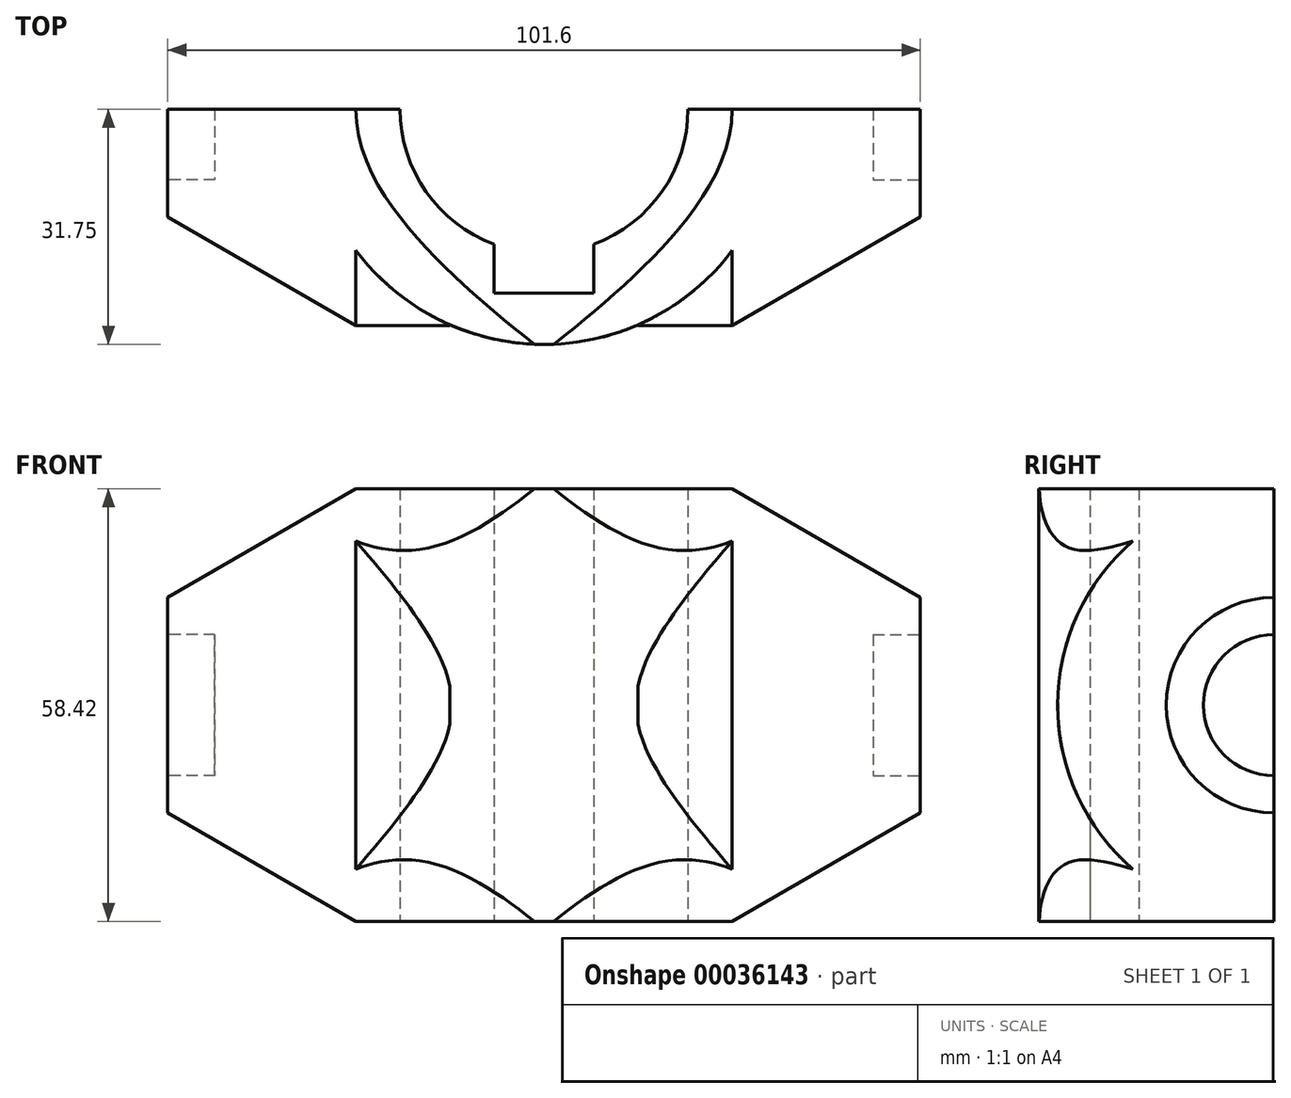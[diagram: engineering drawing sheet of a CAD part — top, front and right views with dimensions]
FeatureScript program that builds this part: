
annotation { "Feature Type Name" : "Feature", "Feature Type Description" : "" }
export const myFeature = defineFeature(function(context is Context, id is Id, definition is map)
    precondition{}
    {
        {
            var Q0;
            Q0=qCreatedBy(makeId("Top.planeOp"),FACE);
            var sketch = newSketch(context, id + "F0", { "sketchPlane" : qUnion([Q0])});
            skPoint(sketch, "E0.rect.middle", {"position": v(0, 0) * mm});
            skArc(sketch, "E1", {"start": v(-31.75, 0) * mm, "mid": v(0, -31.75) * mm, "end": v(31.75, 0) * mm});
            skLineSegment(sketch, "E2", {"start": v(-31.75, 0) * mm, "end": v(31.75, 0) * mm});
            skSolve(sketch);
        }
        {
            var Q0;
            Q0=qCreatedBy(makeId("Right.planeOp"),FACE);
            cPlane(context, id + "F1", {"entities" : qUnion([Q0]), "cplaneType" : CPlaneType.OFFSET, "offset" : 12.7 * mm, "width" : 152.4 * mm, "height" : 152.4 * mm});
        }
        {
            var Q0;
            Q0=qCreatedBy(makeId("Right.planeOp"),FACE);
            cPlane(context, id + "F2", {"entities" : qUnion([Q0]), "cplaneType" : CPlaneType.OFFSET, "offset" : 12.7 * mm, "oppositeDirection" : true, "width" : 152.4 * mm, "height" : 152.4 * mm});
        }
        {
            var Q0;
            Q0 = qSketchRegion(id + "F0", true);
            extrude(context, id + "F3", {"entities" : qUnion([Q0]), "depth" : 58.42 * mm});
        }
        {
            var Q0;
            Q0=qCreatedBy(id+"F2.planeOp",FACE);
            var sketch = newSketch(context, id + "F4", { "sketchPlane" : qUnion([Q0])});
            skArc(sketch, "E3", {"start": v(0, 58.42) * mm, "mid": v(-29.21, 29.21) * mm, "end": v(0, 0) * mm});
            skLineSegment(sketch, "E4", {"start": v(0, 58.42) * mm, "end": v(0, 0) * mm});
            skSolve(sketch);
        }
        {
            var Q0;
            Q0 = qSketchRegion(id + "F4", true);
            extrude(context, id + "F5", {"entities" : qUnion([Q0]), "operationType" : NewBodyOperationType.ADD, "oppositeDirection" : true, "depth" : 38.1 * mm});
        }
        {
            var Q0;
            Q0=makeQuery(id+"F5.opExtrude","CAP_FACE",FACE,{"disambiguationData":[OSD([sQuery(id+"F4.wireOp",EDGE,"E3"),sQuery(id+"F4.wireOp",EDGE,"E4")])],"isStart":false});
            var sketch = newSketch(context, id + "F6", { "sketchPlane" : qUnion([Q0])});
            skArc(sketch, "E5", {"start": v(0, 19.69) * mm, "mid": v(9.53, 29.21) * mm, "end": v(0, 38.73) * mm});
            skLineSegment(sketch, "E6", {"start": v(0, 38.73) * mm, "end": v(0, 19.69) * mm});
            skSolve(sketch);
        }
        {
            var Q0;
            Q0 = qSketchRegion(id + "F6", true);
            extrude(context, id + "F7", {"entities" : qUnion([Q0]), "operationType" : NewBodyOperationType.REMOVE, "oppositeDirection" : true, "depth" : 6.35 * mm});
        }
        {
            var Q0;
            Q0=qCreatedBy(id+"F1.planeOp",FACE);
            var sketch = newSketch(context, id + "F8", { "sketchPlane" : qUnion([Q0])});
            skArc(sketch, "E7", {"start": v(0, 58.42) * mm, "mid": v(-29.2, 29.2) * mm, "end": v(0, 0) * mm});
            skPoint(sketch, "E8.rect.middle", {"position": v(0, 0) * mm});
            skLineSegment(sketch, "E9", {"start": v(0, 58.42) * mm, "end": v(0, 0) * mm});
            skSolve(sketch);
        }
        {
            var Q0;
            Q0 = qSketchRegion(id + "F8", true);
            extrude(context, id + "F9", {"entities" : qUnion([Q0]), "operationType" : NewBodyOperationType.ADD, "depth" : 38.1 * mm});
        }
        {
            var Q0;
            Q0=makeQuery(id+"F9.opExtrude","CAP_FACE",FACE,{"disambiguationData":[OSD([sQuery(id+"F8.wireOp",EDGE,"E7"),sQuery(id+"F8.wireOp",EDGE,"E9")])],"isStart":false});
            var sketch = newSketch(context, id + "F10", { "sketchPlane" : qUnion([Q0])});
            skArc(sketch, "E10", {"start": v(0, 38.73) * mm, "mid": v(-9.53, 29.21) * mm, "end": v(0, 19.69) * mm});
            skLineSegment(sketch, "E11", {"start": v(0, 38.73) * mm, "end": v(0, 19.69) * mm});
            skSolve(sketch);
        }
        {
            var Q0;
            Q0 = qSketchRegion(id + "F10", true);
            extrude(context, id + "F11", {"entities" : qUnion([Q0]), "operationType" : NewBodyOperationType.REMOVE, "oppositeDirection" : true, "depth" : 6.35 * mm});
        }
        {
            var Q0;
            Q0=qCreatedBy(makeId("Top.planeOp"),FACE);
            var sketch = newSketch(context, id + "F12", { "sketchPlane" : qUnion([Q0])});
            skArc(sketch, "E12", {"start": v(-19.43, 0) * mm, "mid": v(-15.94, -11.1) * mm, "end": v(-6.73, -18.23) * mm});
            skLineSegment(sketch, "E13.rect.bottom", {"start": v(6.73, -24.83) * mm, "end": v(-6.73, -24.83) * mm});
            skLineSegment(sketch, "E13.rect.left", {"start": v(6.73, -24.83) * mm, "end": v(6.73, -18.23) * mm});
            skLineSegment(sketch, "E13.rect.right", {"start": v(-6.73, -24.83) * mm, "end": v(-6.73, -18.23) * mm});
            skLineSegment(sketch, "E14", {"start": v(-19.43, 0) * mm, "end": v(19.43, 0) * mm});
            skArc(sketch, "E15.trimOffspring", {"start": v(6.73, -18.23) * mm, "mid": v(15.94, -11.1) * mm, "end": v(19.43, 0) * mm});
            skSolve(sketch);
        }
        {
            var Q0;
            Q0 = qSketchRegion(id + "F12", true);
            extrude(context, id + "F13", {"entities" : qUnion([Q0]), "operationType" : NewBodyOperationType.REMOVE, "depth" : 58.42 * mm});
        }
        {
            var Q0;
            Q0=makeQuery(id+"F5.opExtrude","CAP_EDGE",EDGE,{"disambiguationData":[OSD([sQuery(id+"F4.wireOp",EDGE,"E3")])],"isStart":false});
            chamfer(context, id + "F14", {"entities" : qUnion([Q0]), "chamferType" : ChamferType.OFFSET_ANGLE, "width" : 25.4 * mm, "oppositeDirection" : false, "angle" : 30 * degree, "tangentPropagation" : true});
        }
        {
            var Q0;
            Q0=makeQuery(id+"F9.opExtrude","CAP_EDGE",EDGE,{"disambiguationData":[OSD([sQuery(id+"F8.wireOp",EDGE,"E7")])],"isStart":false});
            chamfer(context, id + "F15", {"entities" : qUnion([Q0]), "chamferType" : ChamferType.OFFSET_ANGLE, "width" : 25.4 * mm, "oppositeDirection" : true, "angle" : 30 * degree, "tangentPropagation" : true});
        }
    });
